# Revit family: STANCA-PLAF_ETANCHE_40W_3600LM_PC_OPALE_IP65_1200MM
name_source: partatom
category: Lighting Fixtures
units: mm (PartAtom-declared; Revit-internal decimal feet)

## family parameters
Always vertical = Yes
Cut with Voids When Loaded = No
Host = Ceiling
Light Source = Yes
OmniClass Number = 23.80.70.11
OmniClass Title = Luminaries for Internal Lighting
Part Type = Normal
Room Calculation Point = No
Round Connector Dimension = Use Diameter
Shared = No

## types (1)
- Type 1
    Alimentation Driver = AC 176-265V
    Alimentation luminaire = 480mA / 75V dc
    Angle d'éclairage = 120°
    Color Filter = 16777215
    Default Elevation = 0 mm  [stored 0 ft]
    Diffuseur = Polycarbonate opale
    Dimensions = 1200x80x50 mm
    Dimming Lamp Color Temperature Shift = <None>
    Driver = Driver GS
    Durée de vie = 30 000 heures
    Emit from Line Length = 610 mm
    IRC = >80
    Maintien du flux = L80B10 (30 000 heures)
    Manufacturer = Lucera - Lucera (c) 06/01/2021 16:38:23 +01:00
    Matériau = Polycarbonate
    Photometric Web File = google_eulumdat_converter.ies
    Puissance nominale = 40W
    SDCM = <2
    Tilt Angle = 90.00°
    URL = https://www.lucera.fr
    Wattage Comments = 40W

note: [stored X ft] marks values corroborated as IEEE doubles in the binary element streams (Revit-internal decimal feet)

## geometry (parser evidence)
native form markers: Sweep x3
no freeform markers — native parametric forms only
